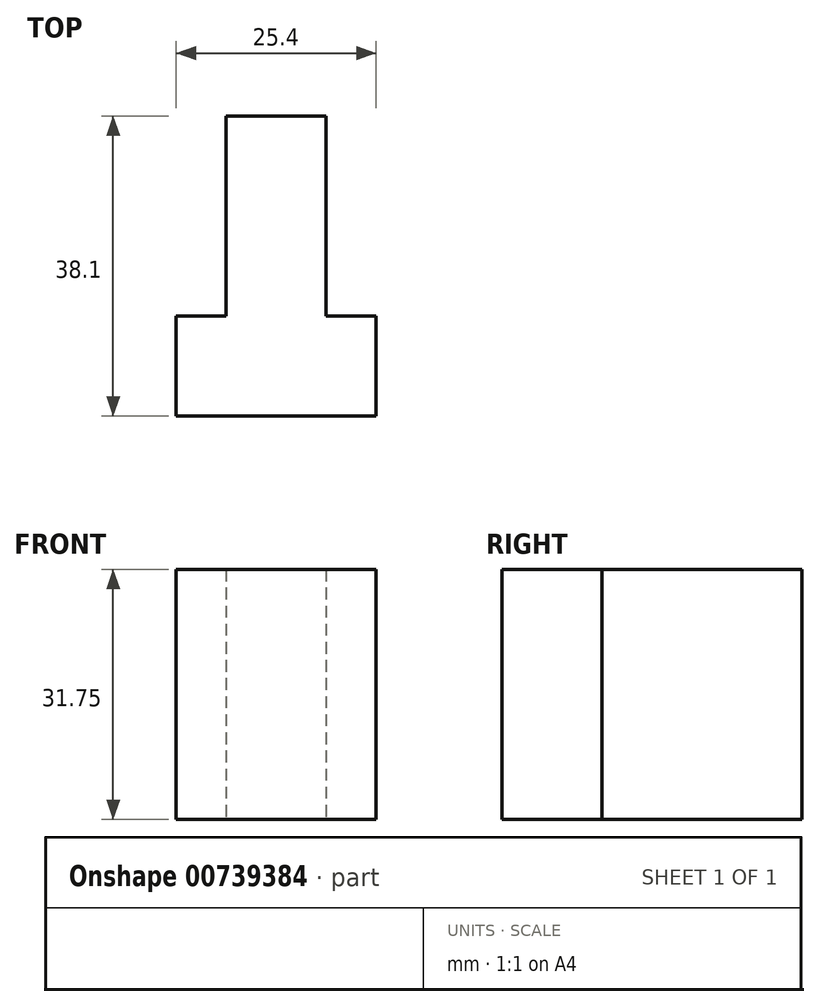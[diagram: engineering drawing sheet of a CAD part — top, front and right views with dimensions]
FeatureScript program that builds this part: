
annotation { "Feature Type Name" : "Feature", "Feature Type Description" : "" }
export const myFeature = defineFeature(function(context is Context, id is Id, definition is map)
    precondition{}
    {
        {
            var Q0;
            Q0=qCreatedBy(makeId("Top.planeOp"),FACE);
            var sketch = newSketch(context, id + "F0", { "sketchPlane" : qUnion([Q0])});
            skLineSegment(sketch, "E0", {"start": v(0, 0) * mm, "end": v(25.4, 0) * mm});
            skLineSegment(sketch, "E1", {"start": v(25.4, 0) * mm, "end": v(25.4, 12.7) * mm});
            skLineSegment(sketch, "E2", {"start": v(25.4, 12.7) * mm, "end": v(19.05, 12.7) * mm});
            skLineSegment(sketch, "E3", {"start": v(19.05, 12.7) * mm, "end": v(19.05, 38.1) * mm});
            skLineSegment(sketch, "E4", {"start": v(19.05, 38.1) * mm, "end": v(6.35, 38.1) * mm});
            skLineSegment(sketch, "E5", {"start": v(6.35, 38.1) * mm, "end": v(6.35, 12.7) * mm});
            skLineSegment(sketch, "E6", {"start": v(6.35, 12.7) * mm, "end": v(0, 12.7) * mm});
            skLineSegment(sketch, "E7", {"start": v(0, 12.7) * mm, "end": v(0, 0) * mm});
            skSolve(sketch);
        }
        {
            var Q0;
            Q0=makeQuery(id+"F0.imprint","IMPRINT",FACE,{"disambiguationData":[TD([[makeQuery(id+"F0.imprint","IMPRINT",EDGE,{"derivedFrom":sQuery(id+"F0.wireOp",EDGE,"E0")}),1.0]])]});
            extrude(context, id + "F1", {"entities" : qUnion([Q0]), "depth" : 31.75 * mm, "offsetDistance" : 25.4 * mm});
        }
    });
